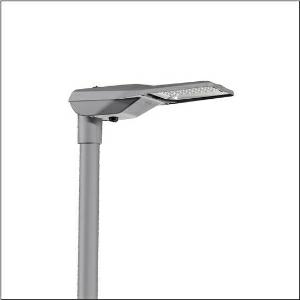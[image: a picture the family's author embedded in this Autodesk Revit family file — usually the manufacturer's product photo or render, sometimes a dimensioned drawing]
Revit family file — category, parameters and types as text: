
# Revit family: streetlight_sl_21_mini___p0_8ab_5xe2r33t08jb_257d
name_source: partatom
category: Lighting Fixtures
units: mm (PartAtom-declared; Revit-internal decimal feet)

## family parameters
Cut with Voids When Loaded = No
Host = Face
Light Source = No
Part Type = Normal
Room Calculation Point = No
Round Connector Dimension = Use Diameter
Shared = No

## types (1)
- --- (1 x LED, 11230 lm, 88.6 W, 3000K)
    Apparent Load = 89 VA
    CIE Flux Codes = 39 72 97 100 100
    Color Rendering = 70
    Color Temperature = 3000K
    Default Elevation = 1800 mm
    Description = Streetlight SL 21 mini, mast luminaire, primary light control with lens, of PMMA, primary optical cover: cover, of toughened safety glass, transparent, light distribution: P0.8aB, light emission: direct distribution, primary light characteristic: asymmetric, installation type: post-top, side-entry, LED, High Power LED, rated luminous flux: 11.230lm, luminous efficacy: 127lm/W, light colour: 730, colour temperature: 3000K, control gear: D4i, control: pre-setting: logarithmic dimming characteristic, flexible luminous flux parameterisation, time-dependent luminous flux control, constant luminous flux control, overheat protection, mains connection: 220..240V, AC, 50/60Hz, start of lifetime: 89W, end of service life: 92W, reduction: 41W, luminaire housing, of diecast aluminium, powder-coated, Siteco® metallic grey (DB 702S), corrosivity category C5 mid according to DIN EN ISO 12944, multi-level sealing system, sealing non-destructively replaceable, inclination adjustable: 0°, 5°, 10°, 15°, please order mast flange separately, length: 628mm, width: 235mm, height: 110mm, mast flange for spigot size: 42mm (side-entry): 5XC10008XM4, 60/48mm (side-entry/post-top): 5XC10108XM2, 76/60mm (side-entry/post-top): 5XC10108XM1, mounting height: 4..8m, Smart Interface below and above, protection rating (complete): IP66, insulation class (complete): insulation class II (safety insulation), certification: CE, ENEC, ENEC+, VDE, impact resistance: IK10, permissible operating ambient temperature for outdoor applications: -40..+50°C, standard-compliant lighting for roads and squares, packaging unit: 1 piece

Light Distribution: P0.8aB
    Height = 110 mm
    Lamp = 1 x LED
    Lamp Light Flux = 11230 lm
    Lamp Power = 88.6 W
    Lamp count = 1
    Length = 625 mm
    Luminous efficacy = 127 lm/W
    Manufacturer = Siteco
    ModVariant = No
    Model = 5XE2R33T08JB
    Number of Poles = 1
    OnlyDefault = Yes
    Power Factor = 1
    Product Name = Streetlight SL 21 mini | P0.8aB
    Product group = mast luminaire | pylon top
    ProductGroupID = 6100
    Protection Class = Protection class II
    Protection Degree = IP 66
    RLX_Detail_Level = 1
    RLX_Emergency_Light_Flux = 0 lm
    RLX_Emergency_Type = 0
    RLX_Emergency_Type_DB = No
    RlxData = <blob elided: 26073 chars, md5=4f334f00>
    Socket = socket
    Standby Power = 0 W
    System Light Flux = 11230 lm
    System Power = 89 W
    Type Comments = factory setting: luminous flux: 100 % | dim-lin: 254 | 915 mA
    Type Image = l_1003514.jpg
    URL = http://relux.com
    VarID = @adj_013167
    Voltage = 0 V
    Weight = 0.00 kg
    Width = 234 mm

## geometry (parser evidence)
native form markers: Blend x4, Sweep x12
no freeform markers — native parametric forms only
